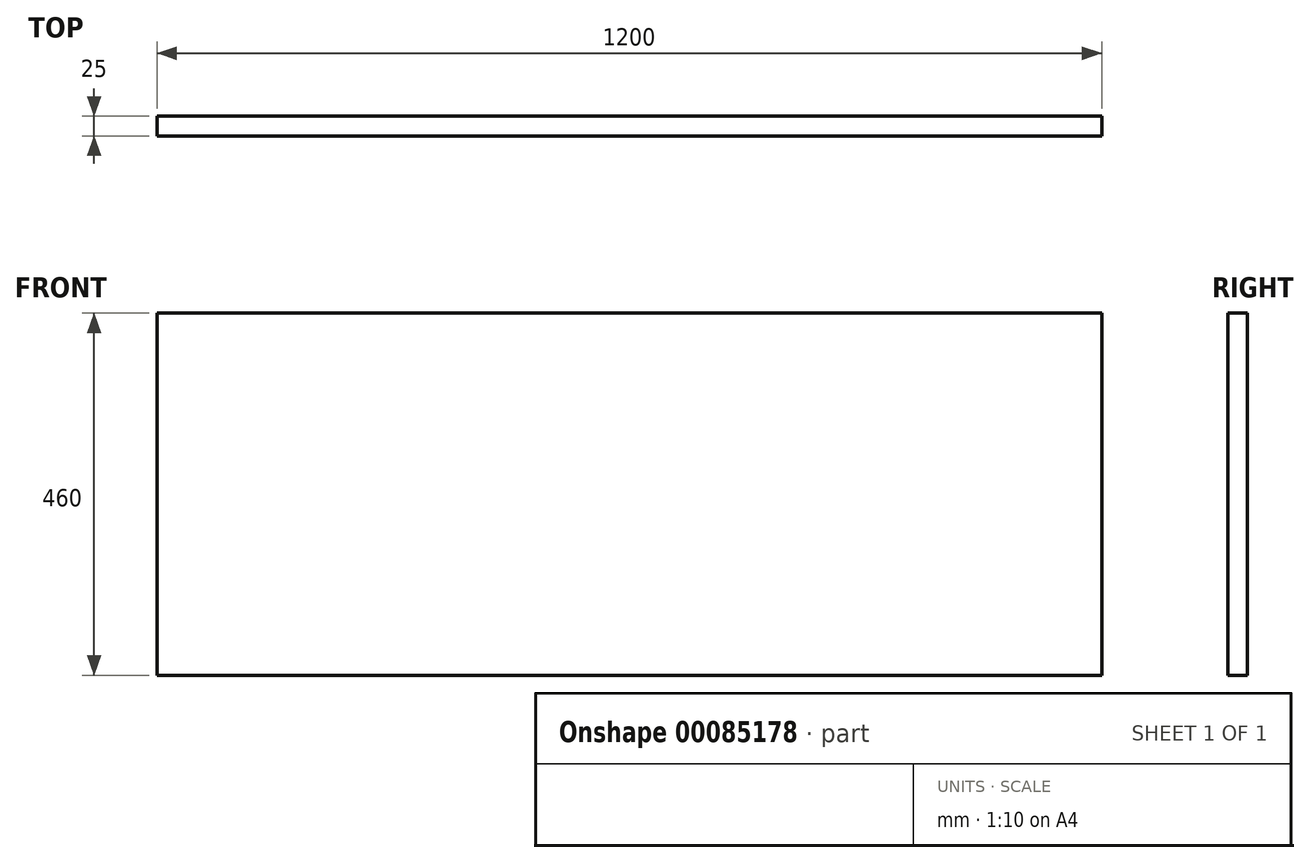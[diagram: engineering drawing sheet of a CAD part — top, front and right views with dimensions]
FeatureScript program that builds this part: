
annotation { "Feature Type Name" : "Feature", "Feature Type Description" : "" }
export const myFeature = defineFeature(function(context is Context, id is Id, definition is map)
    precondition{}
    {
        {
            var Q0;
            Q0=qCreatedBy(makeId("Front.planeOp"),FACE);
            var sketch = newSketch(context, id + "F0", { "sketchPlane" : qUnion([Q0])});
            skLineSegment(sketch, "E0.bottom", {"start": v(600, -230) * mm, "end": v(-600, -230) * mm});
            skLineSegment(sketch, "E0.top", {"start": v(600, 230) * mm, "end": v(-600, 230) * mm});
            skLineSegment(sketch, "E0.left", {"start": v(600, -230) * mm, "end": v(600, 230) * mm});
            skLineSegment(sketch, "E0.right", {"start": v(-600, -230) * mm, "end": v(-600, 230) * mm});
            skPoint(sketch, "E0.middle", {"position": v(0, 0) * mm});
            skSolve(sketch);
        }
        {
            var Q0;
            Q0 = qSketchRegion(id + "F0", true);
            extrude(context, id + "F1", {"entities" : qUnion([Q0]), "depth" : 25 * mm});
        }
    });
